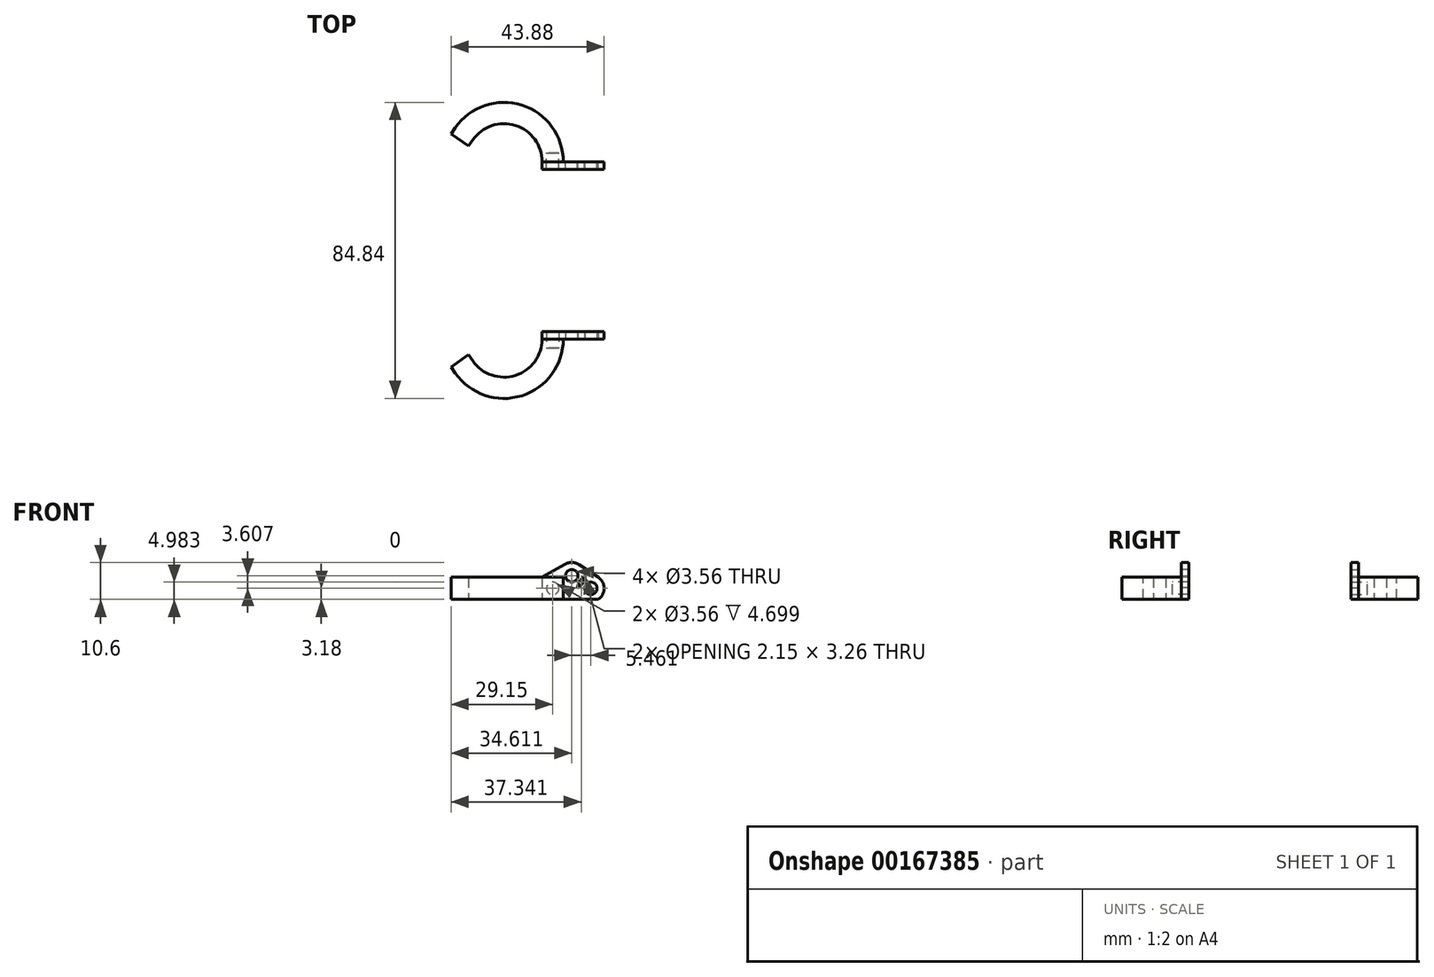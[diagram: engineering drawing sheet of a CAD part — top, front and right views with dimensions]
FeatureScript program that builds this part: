
annotation { "Feature Type Name" : "Feature", "Feature Type Description" : "" }
export const myFeature = defineFeature(function(context is Context, id is Id, definition is map)
    precondition{}
    {
        {
            var Q0;
            Q0=qCreatedBy(makeId("Front.planeOp"),FACE);
            var sketch = newSketch(context, id + "F0", { "sketchPlane" : qUnion([Q0])});
            skLineSegment(sketch, "E0", {"start": v(-13.97, 0) * mm, "end": v(13.97, 0) * mm, "construction": true});
            skLineSegment(sketch, "E1.bottom", {"start": v(17.02, 3.18) * mm, "end": v(10.92, 3.18) * mm});
            skLineSegment(sketch, "E1.top", {"start": v(17.02, -3.18) * mm, "end": v(10.92, -3.18) * mm});
            skLineSegment(sketch, "E1.left", {"start": v(17.02, 3.18) * mm, "end": v(17.02, -3.18) * mm});
            skLineSegment(sketch, "E1.right", {"start": v(10.92, 3.18) * mm, "end": v(10.92, -3.18) * mm});
            skPoint(sketch, "E1.middle", {"position": v(13.97, 0) * mm});
            skCircle(sketch, "E2", {"center": v(13.97, 0) * mm, "radius": 1.78 * mm});
            skLineSegment(sketch, "E3", {"start": v(0, 13.57) * mm, "end": v(0, -13.57) * mm, "construction": true});
            skCircle(sketch, "E4", {"center": v(24.9, 0) * mm, "radius": 1.78 * mm});
            skLineSegment(sketch, "E5", {"start": v(13.97, 0) * mm, "end": v(24.9, 0) * mm, "construction": true});
            skCircle(sketch, "E6", {"center": v(19.43, 3.6) * mm, "radius": 1.78 * mm});
            skPoint(sketch, "E6.centerSnap0", {"position": v(19.43, 0) * mm});
            skCircle(sketch, "E7", {"center": v(19.43, 3.6) * mm, "radius": 3.81 * mm});
            skLineSegment(sketch, "E8", {"start": v(17.02, -3.18) * mm, "end": v(26.98, -3.18) * mm});
            skLineSegment(sketch, "E9", {"start": v(10.92, 3.18) * mm, "end": v(17.56, 6.93) * mm});
            skCircle(sketch, "E10", {"center": v(24.9, 0) * mm, "radius": 3.81 * mm});
            skLineSegment(sketch, "E11", {"start": v(21.53, 6.79) * mm, "end": v(27, 3.18) * mm});
            skSolve(sketch);
        }
        {
            var Q0;
            {var subQ0=sQuery(id+"F0.wireOp",EDGE,"E9");Q0=makeQuery(id+"F0.imprint","IMPRINT",FACE,{"disambiguationData":[TD([[makeQuery(id+"F0.imprint","IMPRINT",EDGE,{"derivedFrom":subQ0}),-1.0]])]});}
            var Q1;
            Q1=makeQuery(id+"F0.imprint","IMPRINT",FACE,{"disambiguationData":[TD([[makeQuery(id+"F0.imprint","IMPRINT",EDGE,{"derivedFrom":sQuery(id+"F0.wireOp",EDGE,"E4")}),-1.0]])]});
            var Q2;
            {var subQ0=sQuery(id+"F0.wireOp",EDGE,"E11");Q2=makeQuery(id+"F0.imprint","IMPRINT",FACE,{"disambiguationData":[TD([[makeQuery(id+"F0.imprint","IMPRINT",EDGE,{"derivedFrom":subQ0}),-1.0]])]});}
            var Q3;
            {var subQ2=sQuery(id+"F0.wireOp",EDGE,"E1.top");Q3=makeQuery(id+"F0.imprint","IMPRINT",FACE,{"disambiguationData":[TD([[makeQuery(id+"F0.imprint","IMPRINT",EDGE,{"derivedFrom":subQ2}),-1.0]])]});}
            var Q4;
            Q4=makeQuery(id+"F0.imprint","IMPRINT",FACE,{"disambiguationData":[TD([[makeQuery(id+"F0.imprint","IMPRINT",EDGE,{"derivedFrom":sQuery(id+"F0.wireOp",EDGE,"E6")}),-1.0]])]});
            var Q5;
            {var subQ0=sQuery(id+"F0.wireOp",EDGE,"E10");var subQ1=sQuery(id+"F0.wireOp",EDGE,"E7");var subQ2=makeQuery(id+"F0.imprint","INTERSECT",VERTEX,{"disambiguationData":[OD(0.0)],"derivedFrom":[subQ1,subQ0]});Q5=makeQuery(id+"F0.imprint","IMPRINT",FACE,{"disambiguationData":[TD([[makeQuery(id+"F0.imprint","IMPRINT",EDGE,{"disambiguationData":[TD([[subQ2,-1.0]])],"derivedFrom":subQ1}),1.0]])]});}
            var Q6;
            {var subQ1=sQuery(id+"F0.wireOp",EDGE,"E1.left");var subQ3=sQuery(id+"F0.wireOp",EDGE,"E7");var subQ4=makeQuery(id+"F0.imprint","INTERSECT",VERTEX,{"derivedFrom":[subQ1,subQ3]});Q6=makeQuery(id+"F0.imprint","IMPRINT",FACE,{"disambiguationData":[TD([[makeQuery(id+"F0.imprint","IMPRINT",EDGE,{"disambiguationData":[TD([[subQ4,-1.0]])],"derivedFrom":subQ3}),-1.0]])]});}
            var Q7;
            {var subQ0=sQuery(id+"F0.wireOp",EDGE,"E1.left");var subQ1=sQuery(id+"F0.wireOp",EDGE,"E1.bottom");var subQ2=makeQuery(id+"F0.imprint","INTERSECT",VERTEX,{"derivedFrom":[subQ1,subQ0]});Q7=makeQuery(id+"F0.imprint","IMPRINT",FACE,{"disambiguationData":[TD([[makeQuery(id+"F0.imprint","IMPRINT",EDGE,{"disambiguationData":[TD([[subQ2,-1.0]])],"derivedFrom":subQ1}),1.0]])]});}
            extrude(context, id + "F1", {"entities" : qUnion([Q0, Q1, Q2, Q3, Q4, Q5, Q6, Q7]), "oppositeDirection" : true, "depth" : 2.16 * mm});
        }
        {
            var Q0;
            {var subQ2=sQuery(id+"F0.wireOp",EDGE,"E1.top");Q0=makeQuery(id+"F0.imprint","IMPRINT",FACE,{"disambiguationData":[TD([[makeQuery(id+"F0.imprint","IMPRINT",EDGE,{"derivedFrom":subQ2}),-1.0]])]});}
            var Q1;
            Q1=makeQuery(id+"F0.imprint","IMPRINT",FACE,{"disambiguationData":[TD([[makeQuery(id+"F0.imprint","IMPRINT",EDGE,{"derivedFrom":sQuery(id+"F0.wireOp",EDGE,"E2")}),1.0]])]});
            var Q2;
            {var subQ0=sQuery(id+"F0.wireOp",EDGE,"E1.left");var subQ1=sQuery(id+"F0.wireOp",EDGE,"E1.bottom");var subQ2=makeQuery(id+"F0.imprint","INTERSECT",VERTEX,{"derivedFrom":[subQ1,subQ0]});Q2=makeQuery(id+"F0.imprint","IMPRINT",FACE,{"disambiguationData":[TD([[makeQuery(id+"F0.imprint","IMPRINT",EDGE,{"disambiguationData":[TD([[subQ2,-1.0]])],"derivedFrom":subQ1}),1.0]])]});}
            var Q3;
            Q3=sQuery(id+"F0.wireOp",EDGE,"E3");
            revolve(context, id + "F2", {"operationType" : NewBodyOperationType.ADD, "entities" : qUnion([Q0, Q1, Q2]), "axis" : qUnion([Q3]), "revolveType" : RevolveType.ONE_DIRECTION, "angle" : 145 * degree});
        }
        {
            var Q0;
            Q0=makeQuery(id+"F0.imprint","IMPRINT",FACE,{"disambiguationData":[TD([[makeQuery(id+"F0.imprint","IMPRINT",EDGE,{"derivedFrom":sQuery(id+"F0.wireOp",EDGE,"E2")}),1.0]])]});
            extrude(context, id + "F3", {"entities" : qUnion([Q0]), "operationType" : NewBodyOperationType.REMOVE, "depth" : 2.54 * mm});
        }
        {
            var Q0;
            Q0=makeQuery(id+"F2.opRevolve","CAP_FACE",FACE,{"disambiguationData":[OSD([sQuery(id+"F0.wireOp",EDGE,"E1.bottom"),sQuery(id+"F0.wireOp",EDGE,"E1.top"),sQuery(id+"F0.wireOp",EDGE,"E1.left"),sQuery(id+"F0.wireOp",EDGE,"E1.right")])],"isStart":false});
            extrude(context, id + "F4", {"entities" : qUnion([Q0]), "operationType" : NewBodyOperationType.ADD, "depth" : 2.16 * mm});
        }
        {
            var Q0;
            Q0=qCreatedBy(makeId("Front.planeOp"),FACE);
            cPlane(context, id + "F5", {"entities" : qUnion([Q0]), "cplaneType" : CPlaneType.OFFSET, "offset" : 25.4 * mm, "oppositeDirection" : true, "width" : 152.4 * mm, "height" : 152.4 * mm});
        }
        {
            var Q0;
            Q0=makeQuery(id+"F1.opExtrude","SWEPT_BODY",BODY,{"disambiguationData":[OSD([sQuery(id+"F0.wireOp",EDGE,"E1.top"),sQuery(id+"F0.wireOp",EDGE,"E1.right"),sQuery(id+"F0.wireOp",EDGE,"E2"),sQuery(id+"F0.wireOp",EDGE,"E4"),sQuery(id+"F0.wireOp",EDGE,"E6"),sQuery(id+"F0.wireOp",EDGE,"E7"),sQuery(id+"F0.wireOp",EDGE,"E8"),sQuery(id+"F0.wireOp",EDGE,"E9"),sQuery(id+"F0.wireOp",EDGE,"E10"),sQuery(id+"F0.wireOp",EDGE,"E11")])]});
            var Q1;
            Q1=qCreatedBy(id+"F5.planeOp",FACE);
            mirror(context, id + "F6", {"entities" : qUnion([Q0]), "mirrorPlane" : qUnion([Q1])});
        }
    });
